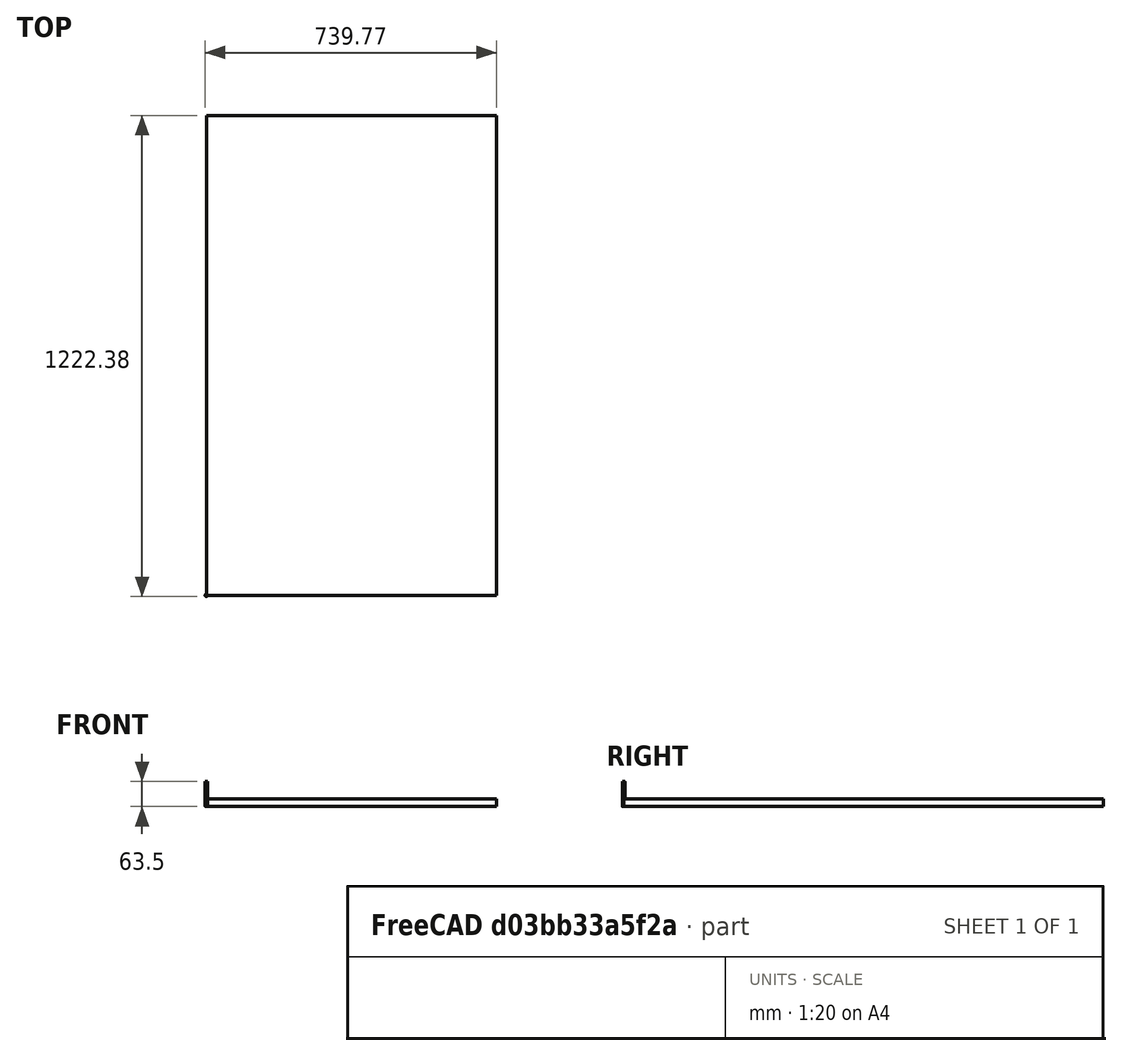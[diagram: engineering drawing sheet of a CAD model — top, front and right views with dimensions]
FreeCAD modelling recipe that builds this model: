
FCSTD DOCUMENT  (FreeCAD 0.21R33771 (Git))
Label: front_panel
License: All rights reserved
LicenseURL: http://en.wikipedia.org/wiki/All_rights_reserved
objects: Path::FeaturePython×9, Part::FeaturePython×6, Part::Box×5, App::DocumentObjectGroup×3, Part::Cylinder×2, Part::MultiFuse×1, App::FeaturePython×1, Mesh::FeaturePython×1, Part::Cut×1
note: 17 computed .brp shape members not serialized (recipe doc carries the construction recipe); baked Part::Feature solids carry a one-line shape summary decoded from their .brp

FEATURE [Part::Box] cube
  AttacherType = Attacher::AttachEngine3D
  Height = 9.6266
  Length = 635
  Width = 635
FEATURE [Part::Cylinder] cylinder
  Angle = 360
  AttacherType = Attacher::AttachEngine3D
  FirstAngle = 0
  Height = 9.6266
  Radius = 25.4
  SecondAngle = 0
FEATURE [Part::FeaturePython] minkowski  # WARN: FeaturePython — macro-defined, semantics opaque (R4)
  Arguments = {'convexity': '0'}
  Children = -> [cube,cylinder]
  Operation = minkowski
  Placement = pos=(25.4,25.4,0) rot=(0,0,1;0rad)
FEATURE [Part::Cylinder] cylinder001
  Angle = 360
  AttacherType = Attacher::AttachEngine3D
  FirstAngle = 0
  Height = 254
  Placement = pos=(342.9,342.9,-127) rot=(0,0,1;0rad)
  Radius = 275.272
  SecondAngle = 0
FEATURE [Part::Box] cube001
  AttacherType = Attacher::AttachEngine3D
  Height = 9.525
  Length = 736.6
  Placement = pos=(-25.4,20.6375,9.7282) rot=(0,0,1;0rad)
  Width = 8.73125
FEATURE [Part::Box] cube002
  AttacherType = Attacher::AttachEngine3D
  Height = 9.525
  Length = 736.6
  Placement = pos=(-25.4,656.431,9.7282) rot=(0,0,1;0rad)
  Width = 8.73125
FEATURE [Part::Box] cube003
  AttacherType = Attacher::AttachEngine3D
  Height = 9.525
  Length = 8.73125
  Placement = pos=(20.6375,29.3687,9.7282) rot=(0,0,1;0rad)
  Width = 627.539
FEATURE [Part::Box] cube004
  AttacherType = Attacher::AttachEngine3D
  Height = 9.525
  Length = 8.73125
  Placement = pos=(656.431,29.3687,9.7282) rot=(0,0,1;0rad)
  Width = 627.539
FEATURE [Part::MultiFuse] union
  Shapes = -> [cylinder001,cube001,cube002,cube003,cube004]
FEATURE [App::FeaturePython] SetupSheet  # Path/CAM operation (typed FeaturePython)
  ClearanceHeightExpression = OpStockZMax+SetupSheet.ClearanceHeightOffset
  ClearanceHeightOffset = 5
  CoolantMode = 0
  CoolantModes = None | Flood | Mist
  FinalDepthExpression = OpFinalDepth
  HorizRapid = 127
  SafeHeightExpression = OpStockZMax+SetupSheet.SafeHeightOffset
  SafeHeightOffset = 3
  StartDepthExpression = OpStartDepth
  StepDownExpression = OpToolDiameter
  VertRapid = 21.1667
FEATURE [Part::FeaturePython] ToolBit  label="Endmill"  # Path/CAM toolbit (typed FeaturePython)
  BitPropertyNames = Chipload | CuttingEdgeHeight | Diameter | Flutes | Length | Material | ShankDiameter | SpindleDirection
  BitShape = <path>
  Chipload = 0
  CuttingEdgeHeight = 30
  Diameter = 5
  Flutes = 0
  Length = 50
  Material = 0
  ShankDiameter = 3
  ShapeName = endmill
  SpindleDirection = 0
FEATURE [Part::FeaturePython] Stock001  # WARN: FeaturePython — macro-defined, semantics opaque (R4)
  Height = 19.2532
  Length = 736.6
  Placement = pos=(3.8147e-07,0.00790062,0) rot=(0,0,1;0rad)
  StockType = CreateBox
  Width = 1219.2
FEATURE [Mesh::FeaturePython] CutMaterial  # WARN: FeaturePython — macro-defined, semantics opaque (R4)
FEATURE [Part::FeaturePython] ToolBit002  label="SpeTool 1/4" Downcut Carbide End Mill"  # Path/CAM toolbit (typed FeaturePython)
  BitPropertyNames = Chipload | CuttingEdgeHeight | Diameter | Flutes | Length | Material | ShankDiameter | SpindleDirection
  BitShape = <path>
  Chipload = 0
  CuttingEdgeHeight = 25.4
  Diameter = 6.35
  File = <userpath>/.config/FreeCAD-tools/Bit/1-4inch_endmill.fctb
  Flutes = 2
  Length = 63.5
  Material = 1
  ShankDiameter = 6.35
  ShapeName = endmill
  SpindleDirection = 0
FEATURE [Path::FeaturePython] TC__SpeTool_1_4__Downcut_Carbide_End_Mill  label="TC: SpeTool 1/4" Downcut Carbide End Mill"  # Path/CAM operation (typed FeaturePython)
  HorizFeed = 0
  HorizRapid = 127
  SpindleDir = 0
  SpindleSpeed = 0
  Tool = -> ToolBit002
  ToolNumber = 1
  VertFeed = 0
  VertRapid = 21.1667
  expr: HorizRapid = SetupSheet.HorizRapid
  expr: VertRapid = SetupSheet.VertRapid
FEATURE [Part::FeaturePython] ToolBit003  label="SpeTool 3/16" Downcut Carbide End Mill"  # Path/CAM toolbit (typed FeaturePython)
  BitPropertyNames = Chipload | CuttingEdgeHeight | Diameter | Flutes | Length | Material | ShankDiameter | SpindleDirection
  BitShape = <path>
  Chipload = 0
  CuttingEdgeHeight = 25.4
  Diameter = 4.7498
  File = <userpath>/.config/FreeCAD-tools/Bit/3-16inch_endmill.fctb
  Flutes = 2
  Length = 63.5
  Material = 1
  ShankDiameter = 6.35
  ShapeName = endmill
  SpindleDirection = 0
FEATURE [Path::FeaturePython] TC__SpeTool_3_16__Downcut_Carbide_End_Mill  label="TC: SpeTool 3/16" Downcut Carbide End Mill"  # Path/CAM operation (typed FeaturePython)
  HorizFeed = 0
  HorizRapid = 127
  SpindleDir = 0
  SpindleSpeed = 0
  Tool = -> ToolBit003
  ToolNumber = 2
  VertFeed = 0
  VertRapid = 21.1667
  expr: HorizRapid = SetupSheet.HorizRapid
  expr: VertRapid = SetupSheet.VertRapid
FEATURE [App::DocumentObjectGroup] Tools
  Group = -> [TC__SpeTool_1_4__Downcut_Carbide_End_Mill,TC__SpeTool_3_16__Downcut_Carbide_End_Mill]
FEATURE [Part::Cut] difference
  Base = -> minkowski
  Tool = -> union
FEATURE [Part::FeaturePython] Clone  label="Model-difference"  # Draft clone (typed FeaturePython)
  AttacherType = Attacher::AttachEngine3D
  Fuse = false
  Objects = -> [difference]
  PathResource = Model
  Placement = pos=(25.4,21.7079,0) rot=(0,0,1;0rad)
  Scale = (1,1,1)
FEATURE [App::DocumentObjectGroup] Model
  Group = -> [Clone]
FEATURE [Path::FeaturePython] Profile  # Path/CAM operation (typed FeaturePython)
  Active = true
  AreaParams:
    Tolerance = 1e-07
    FitArcs = True
    Simplify = False
    CleanDistance = 0.0
    Accuracy = 0.01
    Unit = 1.0
    MinArcPoints = 4
    MaxArcPoints = 100
    ClipperScale = 10000000.0
    Fill = 0
    Coplanar = 0
    Reorient = True
    Outline = False
    Explode = False
    OpenMode = 0
    Deflection = 0.01
    SubjectFill = 0
    ClipFill = 0
    Offset = -3.175
    ExtraPass = 0
    Stepover = 0.0
    LastStepover = 0.0
    JoinType = 0
    EndType = 0
    MiterLimit = 2.0
    RoundPrecision = 0.0
    PocketMode = 0
    ToolRadius = 1.0
    PocketExtraOffset = 0.0
    PocketStepover = 0.0
    PocketLastStepover = 0.0
    FromCenter = False
    Angle = 45.0
    AngleShift = 0.0
    Shift = 0.0
    Thicken = False
    SectionCount = -1
    Stepdown = 1.0
    SectionOffset = 0.0
    SectionTolerance = 1e-07
    SectionMode = 2
    Project = False
  Base = -> [Clone]
  ClearanceHeight = 24.2532
  CoolantMode = 0
  CycleTime = Cycletime Error
  Direction = 0
  FinalDepth = 0
  HandleMultipleFeatures = 0
  JoinType = 0
  MiterLimit = 0.1
  OffsetExtra = 0
  OpFinalDepth = 0
  OpStartDepth = 19.2532
  OpStockZMax = 19.2532
  OpStockZMin = 0
  OpToolDiameter = 6.35
  PathParams = {'orientation': 1, 'feedrate': 0.0, 'feedrate_v': 0.0, 'verbose': True, 'resume_height': 22.2532, 'retraction': 24.2532, 'return_end': True, 'preamble': False}
  SafeHeight = 22.2532
  Side = 1
  SplitArcs = false
  StartDepth = 19.2532
  StartPoint = (0,0,0)
  StepDown = 6.35
  ToolController = -> TC__SpeTool_1_4__Downcut_Carbide_End_Mill
  UseComp = true
  UseStartPoint = false
  processCircles = false
  processHoles = false
  processPerimeter = true
  expr: ClearanceHeight = OpStockZMax + SetupSheet.ClearanceHeightOffset
  expr: FinalDepth = OpFinalDepth
  expr: SafeHeight = OpStockZMax + SetupSheet.SafeHeightOffset
  expr: StartDepth = OpStartDepth
  expr: StepDown = OpToolDiameter
FEATURE [Path::FeaturePython] DressupTag  # Path/CAM operation (typed FeaturePython)
  Angle = 45
  Base = -> Profile
  Disabled = [0,1,2,3,4,5]
  Height = 9.6266
  Positions = (6) [(619.861,470.061,1e-07),(621.616,263.441,1e-07),(478.01,114.874,1e-07),(180.393,166.885,1e-07),(113.722,462.555,1e-07),(257.551,613.883,1e-07)]
  Radius = 0
  SegmentationFactor = 50
  Width = 63.5762
FEATURE [Path::FeaturePython] RampEntryDressup  # Path/CAM operation (typed FeaturePython)
  Angle = 60
  Base = -> Profile
  CustomFeedRate = 0
  DressupStartDepth = 19.2532
  Method = 2
  RampFeedRate = 0
  UseStartDepth = false
FEATURE [Path::FeaturePython] Profile001  # Path/CAM operation (typed FeaturePython)
  Active = true
  AreaParams:
    Tolerance = 1e-07
    FitArcs = True
    Simplify = False
    CleanDistance = 0.0
    Accuracy = 0.01
    Unit = 1.0
    MinArcPoints = 4
    MaxArcPoints = 100
    ClipperScale = 10000000.0
    Fill = 0
    Coplanar = 0
    Reorient = True
    Outline = False
    Explode = False
    OpenMode = 0
    Deflection = 0.01
    SubjectFill = 0
    ClipFill = 0
    Offset = 3.175
    ExtraPass = 0
    Stepover = 0.0
    LastStepover = 0.0
    JoinType = 0
    EndType = 0
    MiterLimit = 2.0
    RoundPrecision = 0.0
    PocketMode = 0
    ToolRadius = 1.0
    PocketExtraOffset = 0.0
    PocketStepover = 0.0
    PocketLastStepover = 0.0
    FromCenter = False
    Angle = 45.0
    AngleShift = 0.0
    Shift = 0.0
    Thicken = False
    SectionCount = -1
    Stepdown = 1.0
    SectionOffset = 0.0
    SectionTolerance = 1e-07
    SectionMode = 2
    Project = False
  Base = -> [Clone]
  ClearanceHeight = 24.2532
  CoolantMode = 0
  CycleTime = Cycletime Error
  Direction = 0
  FinalDepth = 0
  HandleMultipleFeatures = 0
  JoinType = 0
  MiterLimit = 0.1
  OffsetExtra = 0
  OpFinalDepth = 0
  OpStartDepth = 19.2532
  OpStockZMax = 19.2532
  OpStockZMin = 0
  OpToolDiameter = 6.35
  PathParams = {'orientation': 1, 'feedrate': 0.0, 'feedrate_v': 0.0, 'verbose': True, 'resume_height': 22.2532, 'retraction': 24.2532, 'return_end': True, 'preamble': False}
  SafeHeight = 22.2532
  Side = 0
  SplitArcs = false
  StartDepth = 19.2532
  StartPoint = (0,0,0)
  StepDown = 6.35
  ToolController = -> TC__SpeTool_1_4__Downcut_Carbide_End_Mill
  UseComp = true
  UseStartPoint = false
  processCircles = false
  processHoles = false
  processPerimeter = true
  expr: ClearanceHeight = OpStockZMax + SetupSheet.ClearanceHeightOffset
  expr: FinalDepth = OpFinalDepth
  expr: SafeHeight = OpStockZMax + SetupSheet.SafeHeightOffset
  expr: StartDepth = OpStartDepth
  expr: StepDown = OpToolDiameter
FEATURE [Path::FeaturePython] RampEntryDressup001  # Path/CAM operation (typed FeaturePython)
  Angle = 60
  Base = -> Profile001
  CustomFeedRate = 0
  DressupStartDepth = 19.2532
  Method = 2
  RampFeedRate = 0
  UseStartDepth = false
FEATURE [Path::FeaturePython] DressupTag001  # Path/CAM operation (typed FeaturePython)
  Angle = 45
  Base = -> Profile001
  Disabled = [0,1,2,3,4,5,6,7]
  Height = 9.6266
  Positions = (8) [(209.135,709.999,1e-07),(527.334,710.001,1e-07),(713.701,523.41,1e-07),(713.702,205.875,1e-07),(527.465,19.2165,1e-07),(209.266,19.2148,1e-07),+2 more]
  Radius = 0
  SegmentationFactor = 50
  Width = 63.6524
FEATURE [App::DocumentObjectGroup] Operations
  Group = -> [DressupTag,RampEntryDressup,RampEntryDressup001,DressupTag001]
FEATURE [Path::FeaturePython] Job  # Path/CAM operation (typed FeaturePython)
  CycleTime = 00:00:00
  Fixtures = G54
  GeometryTolerance = 0
  JobType = 0
  Model = -> Model
  Operations = -> Operations
  OrderOutputBy = 0
  PostProcessor = 1
  SetupSheet = -> SetupSheet
  SplitOutput = false
  Stock = -> Stock001
  Tools = -> Tools
note: 3 file-system paths scrubbed to <path> (originals preserved in the JSON sidecar)
